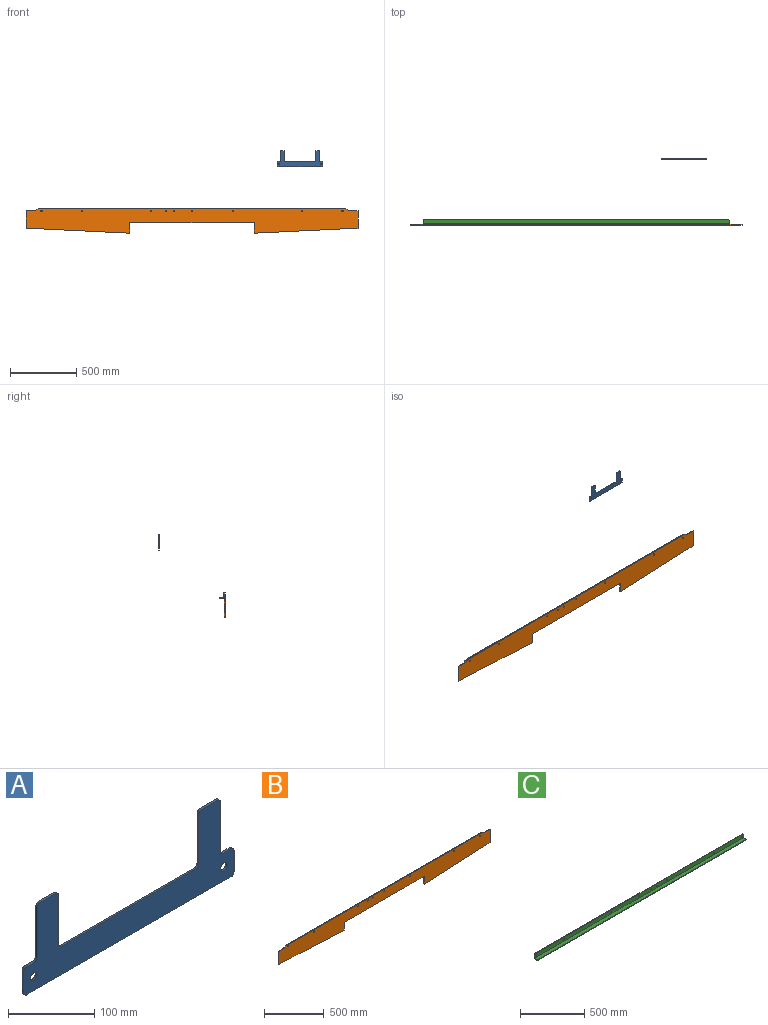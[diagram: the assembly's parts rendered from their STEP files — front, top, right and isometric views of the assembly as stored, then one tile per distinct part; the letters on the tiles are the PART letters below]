
ASSEMBLY  parts=3 mates=1
PART A: 28 faces, bbox 345x3x120 mm
  f0: plane 70x3mm, normal (1,0,0), area 210mm2, adj f14,f15,f19,f25
  f1: plane 25x3mm, normal (0,0,1), area 75mm2, adj f14,f15,f25,f26
  f2: plane 70x3mm, normal (-1,0,0), area 210mm2, adj f14,f15,f26,f27
  f3: plane 220x3mm, normal (0,0,1), area 660mm2, adj f14,f15,f22,f27
  f4: plane 70x3mm, normal (1,0,0), area 210mm2, adj f14,f15,f21,f22
  f5: plane 25x3mm, normal (0,0,1), area 75mm2, adj f14,f15,f21,f24
  f6: plane 70x3mm, normal (-1,0,0), area 210mm2, adj f14,f15,f20,f24
  f7: plane 12.5x3mm, normal (0,0,1), area 37.5mm2, adj f14,f15,f17,f20
  f8: plane 30x3mm, normal (-1,0,0), area 90mm2, adj f14,f15,f17,f18
  f9: plane 335x3mm, normal (0,0,-1), area 1005mm2, adj f14,f15,f18,f23
  f10: plane 30x3mm, normal (1,0,0), area 90mm2, adj f14,f15,f16,f23
  f11: cylinder r=5.5mm len=11mm, axis (0,-1,0), area 103.7mm2, adj f14,f15
  f12: cylinder r=5.5mm len=11mm, axis (0,-1,0), area 103.7mm2, adj f14,f15
  f13: plane 12.5x3mm, normal (0,0,1), area 37.5mm2, adj f14,f15,f16,f19
  f14: plane 345x120mm, normal (0,-1,0), area 19188.5mm2, adj f0,f1,f2,f3,f4,f5,f6,f7
  f15: plane 345x120mm, normal (0,1,0), area 19188.5mm2, adj f0,f1,f2,f3,f4,f5,f6,f7
  f16: cylinder r=5mm len=5mm, axis (0,-1,0), area 23.6mm2, adj f10,f13,f14,f15
  f17: cylinder r=5mm len=5mm, axis (0,1,0), area 23.6mm2, adj f7,f8,f14,f15
  f18: cylinder r=5mm len=5mm, axis (0,1,0), area 23.6mm2, adj f8,f9,f14,f15
  f19: cylinder r=5mm len=5mm, axis (0,1,0), area 23.6mm2, adj f0,f13,f14,f15
  f20: cylinder r=5mm len=5mm, axis (0,1,0), area 23.6mm2, adj f6,f7,f14,f15
  f21: cylinder r=5mm len=5mm, axis (0,1,0), area 23.6mm2, adj f4,f5,f14,f15
  f22: cylinder r=5mm len=5mm, axis (0,1,0), area 23.6mm2, adj f3,f4,f14,f15
  f23: cylinder r=5mm len=5mm, axis (0,-1,0), area 23.6mm2, adj f9,f10,f14,f15
  f24: cylinder r=5mm len=5mm, axis (0,1,0), area 23.6mm2, adj f5,f6,f14,f15
  f25: cylinder r=5mm len=5mm, axis (0,1,0), area 23.6mm2, adj f0,f1,f14,f15
  f26: cylinder r=5mm len=5mm, axis (0,1,0), area 23.6mm2, adj f1,f2,f14,f15
  f27: cylinder r=5mm len=5mm, axis (0,1,0), area 23.6mm2, adj f2,f3,f14,f15
PART B: 29 faces, bbox 2500x6x185 mm
  f0: plane 2294.2x6mm, normal (0,0,1), area 13765.2mm2, adj f23,f24,f27,f28
  f1: plane 19.44x9.72mm, normal (-0.45,0,0.89), area 130.4mm2, adj f23,f24,f26,f27
  f2: plane 61.1x6mm, normal (0,0,1), area 366.6mm2, adj f3,f23,f24,f26
  f3: plane 135x6mm, normal (-1,0,0), area 810mm2, adj f2,f4,f23,f24
  f4: plane 63x6mm, normal (0,0,-1), area 378mm2, adj f3,f5,f23,f24
  f5: plane 717x35mm, normal (-0.05,0,-1), area 4307.1mm2, adj f4,f6,f23,f24
  f6: plane 80x6mm, normal (1,0,0), area 480mm2, adj f5,f7,f23,f24
  f7: plane 940x6mm, normal (0,0,-1), area 5640mm2, adj f6,f8,f23,f24
  f8: plane 80x6mm, normal (-1,0,0), area 480mm2, adj f7,f9,f23,f24
  f9: plane 717x35mm, normal (0.05,0,-1), area 4307.1mm2, adj f8,f10,f23,f24
  f10: plane 63x6mm, normal (0,0,-1), area 378mm2, adj f9,f11,f23,f24
  f11: plane 135x6mm, normal (1,0,0), area 810mm2, adj f10,f12,f23,f24
  f12: plane 61.1x6mm, normal (0,0,1), area 366.6mm2, adj f11,f23,f24,f25
  f13: cylinder r=5.5mm len=11mm, axis (0,-1,0), area 207.3mm2, adj f23,f24
  f14: cylinder r=5.5mm len=11mm, axis (0,-1,0), area 207.3mm2, adj f23,f24
  f15: cylinder r=5.5mm len=11mm, axis (0,-1,0), area 207.3mm2, adj f23,f24
  f16: cylinder r=5.5mm len=11mm, axis (0,-1,0), area 207.3mm2, adj f23,f24
  f17: cylinder r=5.5mm len=11mm, axis (0,-1,0), area 207.3mm2, adj f23,f24
  f18: cylinder r=5.5mm len=11mm, axis (0,-1,0), area 207.3mm2, adj f23,f24
  f19: cylinder r=5.5mm len=11mm, axis (0,-1,0), area 207.3mm2, adj f23,f24
  f20: cylinder r=5.5mm len=11mm, axis (0,-1,0), area 207.3mm2, adj f23,f24
  f21: cylinder r=5.5mm len=11mm, axis (0,-1,0), area 207.3mm2, adj f23,f24
  f22: plane 19.44x9.72mm, normal (0.45,0,0.89), area 130.4mm2, adj f23,f24,f25,f28
  f23: plane 2500x185mm, normal (0,-1,0), area 354479.7mm2, adj f0,f1,f2,f3,f4,f5,f6,f7
  f24: plane 2500x185mm, normal (0,1,0), area 354479.7mm2, adj f0,f1,f2,f3,f4,f5,f6,f7
  f25: cylinder r=25mm len=11.18mm, axis (0,1,0), area 69.5mm2, adj f12,f22,f23,f24
  f26: cylinder r=25mm len=11.18mm, axis (0,1,0), area 69.5mm2, adj f1,f2,f23,f24
  f27: cylinder r=25mm len=11.18mm, axis (0,1,0), area 69.5mm2, adj f0,f1,f23,f24
  f28: cylinder r=25mm len=11.18mm, axis (0,1,0), area 69.5mm2, adj f0,f22,f23,f24
PART C: 27 faces, bbox 2305x39x43 mm
  f0: plane 26.99x6mm, normal (1,0,0), area 161.9mm2, adj f12,f13,f14,f23
  f1: plane 2285x6mm, normal (0,0,1), area 13710mm2, adj f12,f13,f14,f15
  f2: cylinder r=5.5mm len=11mm, axis (0,-1,0), area 207.3mm2, adj f12,f13
  f3: cylinder r=5.5mm len=11mm, axis (0,-1,0), area 207.3mm2, adj f12,f13
  f4: cylinder r=5.5mm len=11mm, axis (0,-1,0), area 207.3mm2, adj f12,f13
  f5: cylinder r=5.5mm len=11mm, axis (0,-1,0), area 207.3mm2, adj f12,f13
  f6: cylinder r=5.5mm len=11mm, axis (0,-1,0), area 207.3mm2, adj f12,f13
  f7: cylinder r=5.5mm len=11mm, axis (0,-1,0), area 207.3mm2, adj f12,f13
  f8: cylinder r=5.5mm len=11mm, axis (0,-1,0), area 207.3mm2, adj f12,f13
  f9: cylinder r=5.5mm len=11mm, axis (0,-1,0), area 207.3mm2, adj f12,f13
  f10: cylinder r=5.5mm len=11mm, axis (0,-1,0), area 207.3mm2, adj f12,f13
  f11: plane 26.99x6mm, normal (-1,0,0), area 161.9mm2, adj f12,f13,f15,f24
  f12: plane 2305x36.99mm, normal (0,-1,0), area 84363.7mm2, adj f0,f1,f2,f3,f4,f5,f6,f7
  f13: plane 2305x36.99mm, normal (0,1,0), area 84363.7mm2, adj f0,f1,f2,f3,f4,f5,f6,f7
  f14: cylinder r=10mm len=10mm, axis (0,1,0), area 94.2mm2, adj f0,f1,f12,f13
  f15: cylinder r=10mm len=10mm, axis (0,-1,0), area 94.2mm2, adj f1,f11,f12,f13
  f16: plane 2285x6mm, normal (0,-1,0), area 13710mm2, adj f19,f20,f21,f22
  f17: plane 22.99x6mm, normal (1,0,0), area 137.9mm2, adj f19,f20,f22,f23
  f18: plane 22.99x6mm, normal (-1,0,0), area 137.9mm2, adj f19,f20,f21,f24
  f19: plane 2305x32.99mm, normal (0,0,1), area 75999mm2, adj f16,f17,f18,f21,f22,f26
  f20: plane 2305x32.99mm, normal (0,0,-1), area 75999mm2, adj f16,f17,f18,f21,f22,f25
  f21: cylinder r=10mm len=10mm, axis (0,0,1), area 94.2mm2, adj f16,f18,f19,f20
  f22: cylinder r=10mm len=10mm, axis (0,0,1), area 94.2mm2, adj f16,f17,f19,f20
  f23: plane 6.01x6.01mm, normal (1,0,0), area 28.4mm2, adj f0,f17,f25,f26
  f24: plane 6.01x6.01mm, normal (-1,0,0), area 28.4mm2, adj f11,f18,f25,f26
  f25: cylinder r=6.01mm len=2305mm, axis (1,0,0), area 21760.3mm2, adj f13,f20,f23,f24
  f26: cylinder r=0.01mm len=2305mm, axis (1,0,0), area 36.2mm2, adj f12,f19,f23,f24
PLACE A t=(539.97,453.37,-256.03)mm
PLACE B t=(-1350.81,-40.71,-756.22)mm
PLACE C rot(axis=(0,0,1),180deg) t=(1052.19,-40.71,-608.22)mm
MATE fastened C.f4 <-> B.f15  axis (0,-1,0) through (1032.19,-40.71,-591.22)mm
